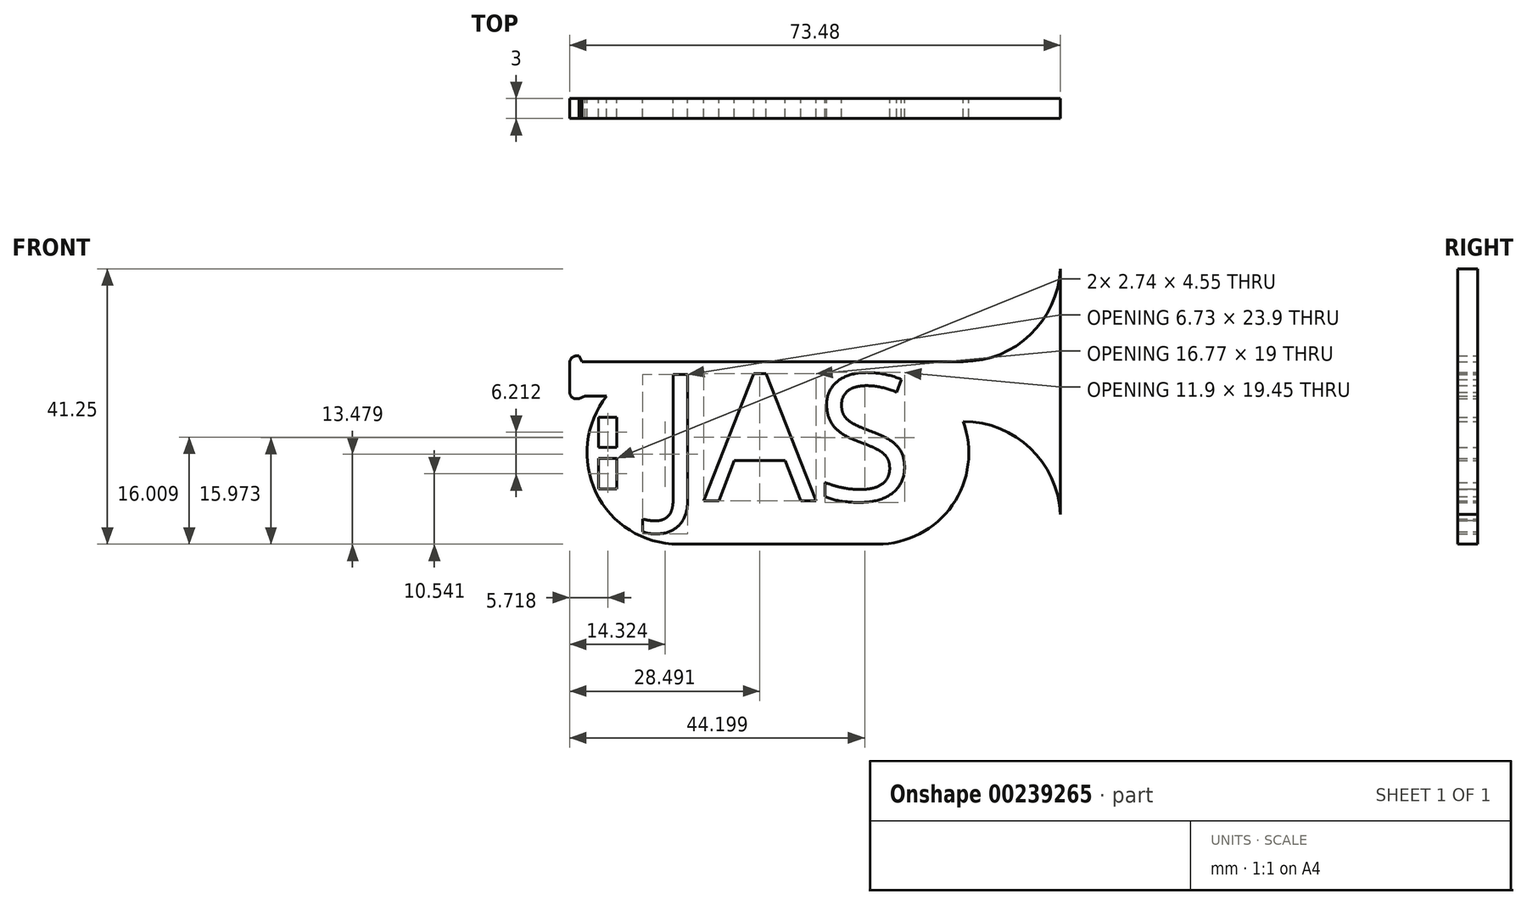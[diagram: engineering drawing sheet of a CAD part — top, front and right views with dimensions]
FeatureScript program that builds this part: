
annotation { "Feature Type Name" : "Feature", "Feature Type Description" : "" }
export const myFeature = defineFeature(function(context is Context, id is Id, definition is map)
    precondition{}
    {
        {
            var Q0;
            Q0=qCreatedBy(makeId("Front.planeOp"),FACE);
            var sketch = newSketch(context, id + "F0", { "sketchPlane" : qUnion([Q0])});
            skArc(sketch, "E0", {"start": v(-10.7, 8.5) * mm, "mid": v(-12.3, -5.95) * mm, "end": v(0, -13.67) * mm});
            skArc(sketch, "E1", {"start": v(29.83, -13.67) * mm, "mid": v(41.04, -7.82) * mm, "end": v(42.66, 4.72) * mm});
            skLineSegment(sketch, "E2", {"start": v(0, 13.67) * mm, "end": v(29.83, 13.67) * mm});
            skLineSegment(sketch, "E3", {"start": v(0, -13.67) * mm, "end": v(29.83, -13.67) * mm});
            skLineSegment(sketch, "E4", {"start": v(0, 13.67) * mm, "end": v(-14.43, 13.67) * mm});
            skLineSegment(sketch, "E5", {"start": v(-14.43, 13.67) * mm, "end": v(-14.83, 14.51) * mm});
            skLineSegment(sketch, "E6", {"start": v(-14.83, 14.51) * mm, "end": v(-15.27, 14.51) * mm});
            skLineSegment(sketch, "E7", {"start": v(-16.27, 13.51) * mm, "end": v(-16.27, 9.1) * mm});
            skLineSegment(sketch, "E8", {"start": v(-15.27, 8.1) * mm, "end": v(-14.83, 8.1) * mm});
            skLineSegment(sketch, "E9", {"start": v(-14.83, 8.1) * mm, "end": v(-13.99, 8.5) * mm});
            skLineSegment(sketch, "E10", {"start": v(-13.99, 8.5) * mm, "end": v(-10.7, 8.5) * mm});
            skPoint(sketch, "E11.visualSharp", {"position": v(-16.27, 14.51) * mm});
            skArc(sketch, "E11.filletArc", {"start": v(-15.27, 14.51) * mm, "mid": v(-15.98, 14.22) * mm, "end": v(-16.27, 13.51) * mm});
            skPoint(sketch, "E12.visualSharp", {"position": v(-16.27, 8.1) * mm});
            skArc(sketch, "E12.filletArc", {"start": v(-16.27, 9.1) * mm, "mid": v(-15.98, 8.4) * mm, "end": v(-15.27, 8.1) * mm});
            skLineSegment(sketch, "E13", {"start": v(29.83, 13.67) * mm, "end": v(42.66, 13.67) * mm});
            skLineSegment(sketch, "E14", {"start": v(42.66, 4.72) * mm, "end": v(42.66, 4.72) * mm});
            skLineSegment(sketch, "E15", {"start": v(42.66, 13.67) * mm, "end": v(42.66, 4.72) * mm, "construction": true});
            skArc(sketch, "E16", {"start": v(42.66, 13.67) * mm, "mid": v(53.19, 18.17) * mm, "end": v(57.21, 28.88) * mm});
            skArc(sketch, "E17", {"start": v(57.21, -9.2) * mm, "mid": v(52.73, 0.68) * mm, "end": v(42.66, 4.72) * mm});
            skLineSegment(sketch, "E18", {"start": v(42.66, 28.23) * mm, "end": v(42.66, -9.84) * mm, "construction": true});
            skLineSegment(sketch, "E19", {"start": v(57.21, 28.88) * mm, "end": v(57.21, -9.2) * mm});
            skLineSegment(sketch, "E20.bottom", {"start": v(-11.92, 5.36) * mm, "end": v(-9.18, 5.36) * mm});
            skLineSegment(sketch, "E20.top", {"start": v(-11.92, -5.4) * mm, "end": v(-9.18, -5.4) * mm});
            skLineSegment(sketch, "E20.left", {"start": v(-11.92, 5.36) * mm, "end": v(-11.92, 0.8) * mm});
            skLineSegment(sketch, "E20.right", {"start": v(-9.18, 5.36) * mm, "end": v(-9.18, 0.8) * mm});
            skPoint(sketch, "E21.endSnap0", {"position": v(-9.18, -0.02) * mm});
            skLineSegment(sketch, "E22.trimOffspring", {"start": v(-11.92, -0.86) * mm, "end": v(-11.92, -5.4) * mm});
            skLineSegment(sketch, "E23.trimOffspring", {"start": v(-9.18, -0.86) * mm, "end": v(-9.18, -5.4) * mm});
            skLineSegment(sketch, "E24", {"start": v(-11.92, 0.8) * mm, "end": v(-9.18, 0.8) * mm});
            skLineSegment(sketch, "E25", {"start": v(-11.92, -0.86) * mm, "end": v(-9.18, -0.86) * mm});
            skPoint(sketch, "E26.orphan", {"position": v(-9.18, 0) * mm});
            skPoint(sketch, "E27.orphan", {"position": v(-11.92, -0.02) * mm});
            skText(sketch, "E28", { "text": "JAS\n", "fontName": "OpenSans-Regular.ttf"});
            const initialGuessF0  = {"E28": [-0.00324, -0.00716, 1, 0, 0.01908]};
            skSetInitialGuess(sketch, initialGuessF0);
            skSolve(sketch);
        }
        {
            var Q0;
            Q0=makeQuery(id+"F0.imprint","IMPRINT",FACE,{"disambiguationData":[TD([[makeQuery(id+"F0.imprint","IMPRINT",EDGE,{"derivedFrom":sQuery(id+"F0.wireOp",EDGE,"E0")}),1.0]])]});
            extrude(context, id + "F1", {"entities" : qUnion([Q0]), "depth" : 3 * mm});
        }
    });
